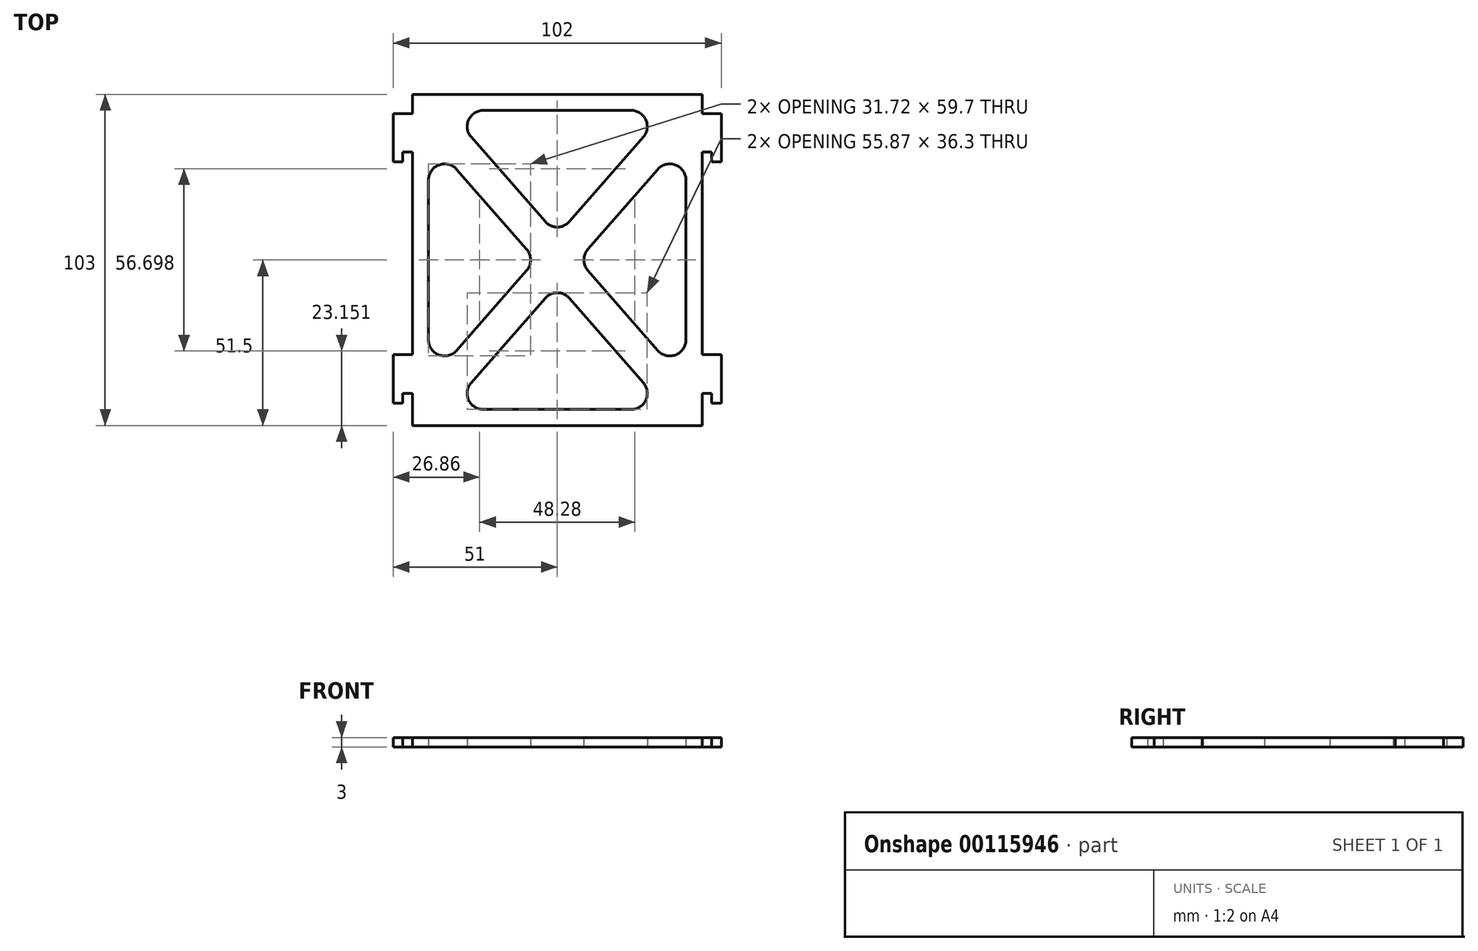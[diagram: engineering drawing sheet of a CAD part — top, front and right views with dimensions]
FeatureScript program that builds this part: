
annotation { "Feature Type Name" : "Feature", "Feature Type Description" : "" }
export const myFeature = defineFeature(function(context is Context, id is Id, definition is map)
    precondition{}
    {
        {
            var Q0;
            Q0=qCreatedBy(makeId("Top.planeOp"),FACE);
            var sketch = newSketch(context, id + "F0", { "sketchPlane" : qUnion([Q0])});
            skLineSegment(sketch, "E0.bottom", {"start": v(45, -51.5) * mm, "end": v(-45, -51.5) * mm});
            skLineSegment(sketch, "E0.top", {"start": v(45, 51.5) * mm, "end": v(-45, 51.5) * mm});
            skLineSegment(sketch, "E0.left", {"start": v(45, -51.5) * mm, "end": v(45, 51.5) * mm});
            skLineSegment(sketch, "E0.right", {"start": v(-45, -51.5) * mm, "end": v(-45, 51.5) * mm});
            skPoint(sketch, "E0.middle", {"position": v(0, 0) * mm});
            skLineSegment(sketch, "E1", {"start": v(-45, 51.5) * mm, "end": v(45, -51.5) * mm, "construction": true});
            skLineSegment(sketch, "E2", {"start": v(45, 51.5) * mm, "end": v(-45, -51.5) * mm, "construction": true});
            skLineSegment(sketch, "E3.0", {"start": v(-31.23, 28.15) * mm, "end": v(-9.51, 3.29) * mm});
            skLineSegment(sketch, "E4.0", {"start": v(-40, -24.86) * mm, "end": v(-40, 24.86) * mm});
            skLineSegment(sketch, "E5.0", {"start": v(-9.51, -3.29) * mm, "end": v(-31.23, -28.15) * mm});
            skArc(sketch, "E6.filletArc", {"start": v(-31.23, 28.15) * mm, "mid": v(-36.76, 29.54) * mm, "end": v(-40, 24.86) * mm});
            skArc(sketch, "E7.filletArc", {"start": v(-9.51, -3.29) * mm, "mid": v(-8.28, 0) * mm, "end": v(-9.51, 3.29) * mm});
            skArc(sketch, "E8.filletArc", {"start": v(-40, -24.86) * mm, "mid": v(-36.76, -29.54) * mm, "end": v(-31.23, -28.15) * mm});
            skLineSegment(sketch, "E9.0", {"start": v(26.75, 38.21) * mm, "end": v(3.77, 11.9) * mm});
            skLineSegment(sketch, "E10.0", {"start": v(-26.75, 38.21) * mm, "end": v(-3.77, 11.9) * mm});
            skLineSegment(sketch, "E11.0", {"start": v(22.98, 46.5) * mm, "end": v(-22.98, 46.5) * mm});
            skArc(sketch, "E12.filletArc", {"start": v(-22.98, 46.5) * mm, "mid": v(-27.53, 43.57) * mm, "end": v(-26.75, 38.21) * mm});
            skArc(sketch, "E13.filletArc", {"start": v(26.75, 38.21) * mm, "mid": v(27.53, 43.57) * mm, "end": v(22.98, 46.5) * mm});
            skArc(sketch, "E14.filletArc", {"start": v(-3.77, 11.9) * mm, "mid": v(0, 10.2) * mm, "end": v(3.77, 11.9) * mm});
            skLineSegment(sketch, "E15.MirrorCS", {"start": v(-26.75, -38.21) * mm, "end": v(-3.77, -11.9) * mm});
            skArc(sketch, "E16.MirrorCS", {"start": v(-22.98, -46.5) * mm, "mid": v(-27.53, -43.57) * mm, "end": v(-26.75, -38.21) * mm});
            skLineSegment(sketch, "E17.MirrorCS", {"start": v(22.98, -46.5) * mm, "end": v(-22.98, -46.5) * mm});
            skArc(sketch, "E18.MirrorCS", {"start": v(26.75, -38.21) * mm, "mid": v(27.53, -43.57) * mm, "end": v(22.98, -46.5) * mm});
            skLineSegment(sketch, "E19.MirrorCS", {"start": v(26.75, -38.21) * mm, "end": v(3.77, -11.9) * mm});
            skArc(sketch, "E20.MirrorCS", {"start": v(-3.77, -11.9) * mm, "mid": v(0, -10.2) * mm, "end": v(3.77, -11.9) * mm});
            skLineSegment(sketch, "E21.MirrorCS", {"start": v(31.23, 28.15) * mm, "end": v(9.51, 3.29) * mm});
            skArc(sketch, "E22.MirrorCS", {"start": v(31.23, 28.15) * mm, "mid": v(36.76, 29.54) * mm, "end": v(40, 24.86) * mm});
            skLineSegment(sketch, "E23.MirrorCS", {"start": v(40, -24.86) * mm, "end": v(40, 24.86) * mm});
            skArc(sketch, "E24.MirrorCS", {"start": v(40, -24.86) * mm, "mid": v(36.76, -29.54) * mm, "end": v(31.23, -28.15) * mm});
            skLineSegment(sketch, "E25.MirrorCS", {"start": v(9.51, -3.29) * mm, "end": v(31.23, -28.15) * mm});
            skArc(sketch, "E26.MirrorCS", {"start": v(9.51, -3.29) * mm, "mid": v(8.28, 0) * mm, "end": v(9.51, 3.29) * mm});
            skSolve(sketch);
        }
        {
            var Q0;
            Q0=makeQuery(id+"F0.imprint","IMPRINT",FACE,{"disambiguationData":[TD([[makeQuery(id+"F0.imprint","IMPRINT",EDGE,{"derivedFrom":sQuery(id+"F0.wireOp",EDGE,"E0.bottom")}),-1.0]])]});
            extrude(context, id + "F1", {"entities" : qUnion([Q0]), "depth" : 3 * mm});
        }
        {
            var Q0;
            Q0=makeQuery(id+"F1.opExtrude","CAP_FACE",FACE,{"disambiguationData":[OSD([sQuery(id+"F0.wireOp",EDGE,"E0.bottom"),sQuery(id+"F0.wireOp",EDGE,"E0.top"),sQuery(id+"F0.wireOp",EDGE,"E0.left"),sQuery(id+"F0.wireOp",EDGE,"E0.right"),sQuery(id+"F0.wireOp",EDGE,"E3.0"),sQuery(id+"F0.wireOp",EDGE,"E4.0"),sQuery(id+"F0.wireOp",EDGE,"E5.0"),sQuery(id+"F0.wireOp",EDGE,"E6.filletArc"),sQuery(id+"F0.wireOp",EDGE,"E7.filletArc"),sQuery(id+"F0.wireOp",EDGE,"E8.filletArc"),sQuery(id+"F0.wireOp",EDGE,"E9.0"),sQuery(id+"F0.wireOp",EDGE,"E10.0"),sQuery(id+"F0.wireOp",EDGE,"E11.0"),sQuery(id+"F0.wireOp",EDGE,"E12.filletArc"),sQuery(id+"F0.wireOp",EDGE,"E13.filletArc"),sQuery(id+"F0.wireOp",EDGE,"E14.filletArc"),sQuery(id+"F0.wireOp",EDGE,"E15.MirrorCS"),sQuery(id+"F0.wireOp",EDGE,"E16.MirrorCS"),sQuery(id+"F0.wireOp",EDGE,"E17.MirrorCS"),sQuery(id+"F0.wireOp",EDGE,"E18.MirrorCS"),sQuery(id+"F0.wireOp",EDGE,"E19.MirrorCS"),sQuery(id+"F0.wireOp",EDGE,"E20.MirrorCS"),sQuery(id+"F0.wireOp",EDGE,"E21.MirrorCS"),sQuery(id+"F0.wireOp",EDGE,"E22.MirrorCS"),sQuery(id+"F0.wireOp",EDGE,"E23.MirrorCS"),sQuery(id+"F0.wireOp",EDGE,"E24.MirrorCS"),sQuery(id+"F0.wireOp",EDGE,"E25.MirrorCS"),sQuery(id+"F0.wireOp",EDGE,"E26.MirrorCS")])],"isStart":false});
            var sketch = newSketch(context, id + "F2", { "sketchPlane" : qUnion([Q0])});
            skLineSegment(sketch, "E27.bottom", {"start": v(-45, 45.5) * mm, "end": v(-51, 45.5) * mm});
            skLineSegment(sketch, "E27.top", {"start": v(-48, 30.5) * mm, "end": v(-51, 30.5) * mm});
            skLineSegment(sketch, "E27.left", {"start": v(-45, 45.5) * mm, "end": v(-45, 33.5) * mm});
            skLineSegment(sketch, "E27.right", {"start": v(-51, 45.5) * mm, "end": v(-51, 30.5) * mm});
            skLineSegment(sketch, "E28.bottom", {"start": v(-45, 33.5) * mm, "end": v(-48, 33.5) * mm});
            skLineSegment(sketch, "E28.right", {"start": v(-48, 33.5) * mm, "end": v(-48, 30.5) * mm});
            skPoint(sketch, "E29.orphan", {"position": v(-45, 30.5) * mm});
            skLineSegment(sketch, "E30.bottom", {"start": v(-51, -29.5) * mm, "end": v(-45, -29.5) * mm});
            skLineSegment(sketch, "E30.top", {"start": v(-51, -44.5) * mm, "end": v(-48, -44.5) * mm});
            skLineSegment(sketch, "E30.left", {"start": v(-51, -29.5) * mm, "end": v(-51, -44.5) * mm});
            skLineSegment(sketch, "E30.right", {"start": v(-45, -29.5) * mm, "end": v(-45, -41.5) * mm});
            skLineSegment(sketch, "E31.bottom", {"start": v(-45, -41.5) * mm, "end": v(-48, -41.5) * mm});
            skLineSegment(sketch, "E31.right", {"start": v(-48, -41.5) * mm, "end": v(-48, -44.5) * mm});
            skPoint(sketch, "E32.orphan", {"position": v(-45, -44.5) * mm});
            skLineSegment(sketch, "E33.MirrorCS", {"start": v(45, -41.5) * mm, "end": v(48, -41.5) * mm});
            skLineSegment(sketch, "E34.MirrorCS", {"start": v(48, -41.5) * mm, "end": v(48, -44.5) * mm});
            skLineSegment(sketch, "E35.MirrorCS", {"start": v(48, 30.5) * mm, "end": v(51, 30.5) * mm});
            skLineSegment(sketch, "E36.MirrorCS", {"start": v(48, 33.5) * mm, "end": v(48, 30.5) * mm});
            skLineSegment(sketch, "E37.MirrorCS", {"start": v(51, -44.5) * mm, "end": v(48, -44.5) * mm});
            skLineSegment(sketch, "E38.MirrorCS", {"start": v(45, 33.5) * mm, "end": v(48, 33.5) * mm});
            skLineSegment(sketch, "E39.MirrorCS", {"start": v(51, 45.5) * mm, "end": v(51, 30.5) * mm});
            skLineSegment(sketch, "E40.MirrorCS", {"start": v(45, 45.5) * mm, "end": v(51, 45.5) * mm});
            skPoint(sketch, "E41.MirrorP", {"position": v(45, -44.5) * mm});
            skPoint(sketch, "E42.MirrorP", {"position": v(45, 30.5) * mm});
            skLineSegment(sketch, "E43.MirrorCS", {"start": v(51, -29.5) * mm, "end": v(51, -44.5) * mm});
            skLineSegment(sketch, "E44.MirrorCS", {"start": v(45, 45.5) * mm, "end": v(45, 33.5) * mm});
            skLineSegment(sketch, "E45.MirrorCS", {"start": v(45, -29.5) * mm, "end": v(45, -41.5) * mm});
            skLineSegment(sketch, "E46.MirrorCS", {"start": v(51, -29.5) * mm, "end": v(45, -29.5) * mm});
            skSolve(sketch);
        }
        {
            var Q0;
            Q0=makeQuery(id+"F2.imprint","IMPRINT",FACE,{"disambiguationData":[TD([[makeQuery(id+"F2.imprint","IMPRINT",EDGE,{"derivedFrom":sQuery(id+"F2.wireOp",EDGE,"E27.bottom")}),1.0]])]});
            var Q1;
            Q1=makeQuery(id+"F2.imprint","IMPRINT",FACE,{"disambiguationData":[TD([[makeQuery(id+"F2.imprint","IMPRINT",EDGE,{"derivedFrom":sQuery(id+"F2.wireOp",EDGE,"E35.MirrorCS")}),1.0]])]});
            var Q2;
            Q2=makeQuery(id+"F2.imprint","IMPRINT",FACE,{"disambiguationData":[TD([[makeQuery(id+"F2.imprint","IMPRINT",EDGE,{"derivedFrom":sQuery(id+"F2.wireOp",EDGE,"E33.MirrorCS")}),1.0]])]});
            var Q3;
            Q3=makeQuery(id+"F2.imprint","IMPRINT",FACE,{"disambiguationData":[TD([[makeQuery(id+"F2.imprint","IMPRINT",EDGE,{"derivedFrom":sQuery(id+"F2.wireOp",EDGE,"E30.bottom")}),-1.0]])]});
            var Q4;
            Q4=makeQuery(id+"F1.opExtrude","CAP_FACE",FACE,{"disambiguationData":[OSD([sQuery(id+"F0.wireOp",EDGE,"E0.bottom"),sQuery(id+"F0.wireOp",EDGE,"E0.top"),sQuery(id+"F0.wireOp",EDGE,"E0.left"),sQuery(id+"F0.wireOp",EDGE,"E0.right"),sQuery(id+"F0.wireOp",EDGE,"E3.0"),sQuery(id+"F0.wireOp",EDGE,"E4.0"),sQuery(id+"F0.wireOp",EDGE,"E5.0"),sQuery(id+"F0.wireOp",EDGE,"E6.filletArc"),sQuery(id+"F0.wireOp",EDGE,"E7.filletArc"),sQuery(id+"F0.wireOp",EDGE,"E8.filletArc"),sQuery(id+"F0.wireOp",EDGE,"E9.0"),sQuery(id+"F0.wireOp",EDGE,"E10.0"),sQuery(id+"F0.wireOp",EDGE,"E11.0"),sQuery(id+"F0.wireOp",EDGE,"E12.filletArc"),sQuery(id+"F0.wireOp",EDGE,"E13.filletArc"),sQuery(id+"F0.wireOp",EDGE,"E14.filletArc"),sQuery(id+"F0.wireOp",EDGE,"E15.MirrorCS"),sQuery(id+"F0.wireOp",EDGE,"E16.MirrorCS"),sQuery(id+"F0.wireOp",EDGE,"E17.MirrorCS"),sQuery(id+"F0.wireOp",EDGE,"E18.MirrorCS"),sQuery(id+"F0.wireOp",EDGE,"E19.MirrorCS"),sQuery(id+"F0.wireOp",EDGE,"E20.MirrorCS"),sQuery(id+"F0.wireOp",EDGE,"E21.MirrorCS"),sQuery(id+"F0.wireOp",EDGE,"E22.MirrorCS"),sQuery(id+"F0.wireOp",EDGE,"E23.MirrorCS"),sQuery(id+"F0.wireOp",EDGE,"E24.MirrorCS"),sQuery(id+"F0.wireOp",EDGE,"E25.MirrorCS"),sQuery(id+"F0.wireOp",EDGE,"E26.MirrorCS")])],"isStart":true});
            extrude(context, id + "F3", {"entities" : qUnion([Q0, Q1, Q2, Q3]), "operationType" : NewBodyOperationType.ADD, "endBound" : BoundingType.UP_TO_SURFACE, "oppositeDirection" : true, "endBoundEntityFace" : qUnion([Q4]), "depth" : 25 * mm});
        }
    });
